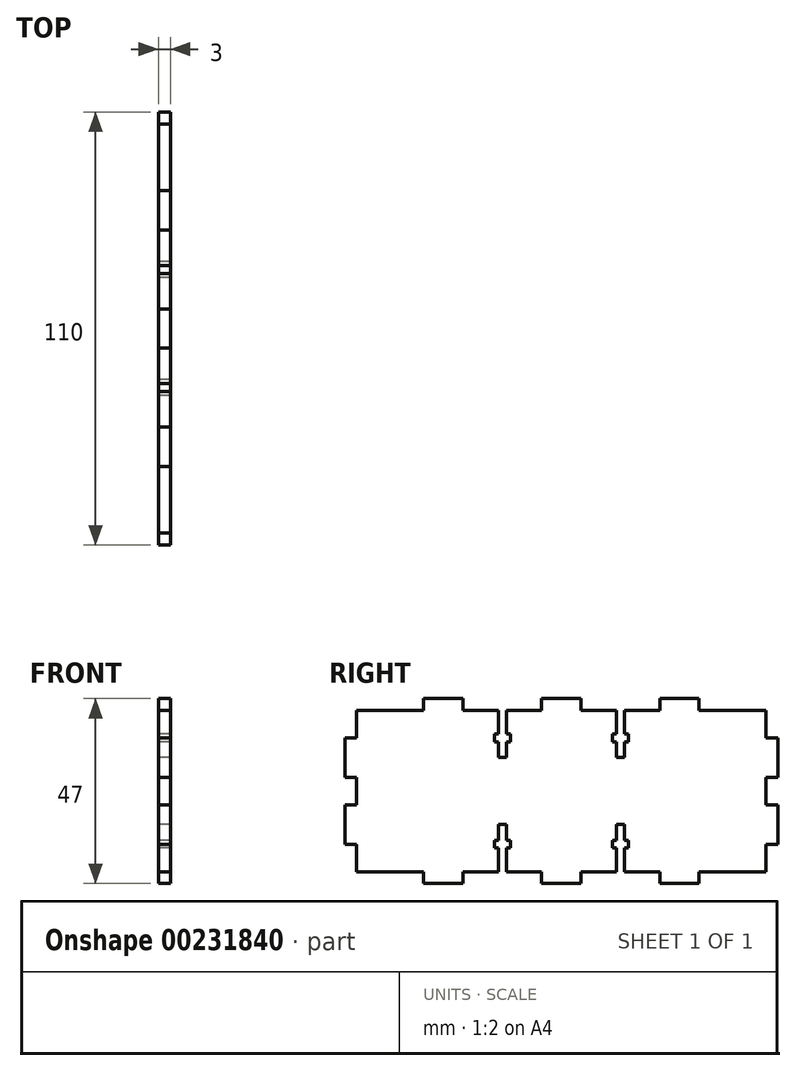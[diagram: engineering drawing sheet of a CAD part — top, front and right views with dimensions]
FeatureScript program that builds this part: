
annotation { "Feature Type Name" : "Feature", "Feature Type Description" : "" }
export const myFeature = defineFeature(function(context is Context, id is Id, definition is map)
    precondition{}
    {
        {
            var Q0;
            Q0=qCreatedBy(makeId("Right.planeOp"),FACE);
            var sketch = newSketch(context, id + "F0", { "sketchPlane" : qUnion([Q0])});
            skLineSegment(sketch, "E0", {"start": v(0, 0) * mm, "end": v(0, 7) * mm});
            skLineSegment(sketch, "E1", {"start": v(0, 7) * mm, "end": v(3, 7) * mm});
            skLineSegment(sketch, "E2", {"start": v(3, 7) * mm, "end": v(3, 17) * mm});
            skLineSegment(sketch, "E3", {"start": v(3, 17) * mm, "end": v(0, 17) * mm});
            skLineSegment(sketch, "E4", {"start": v(0, 17) * mm, "end": v(0, 24) * mm});
            skLineSegment(sketch, "E5", {"start": v(0, 24) * mm, "end": v(3, 24) * mm});
            skLineSegment(sketch, "E6", {"start": v(3, 24) * mm, "end": v(3, 34) * mm});
            skLineSegment(sketch, "E7", {"start": v(3, 34) * mm, "end": v(0, 34) * mm});
            skLineSegment(sketch, "E8", {"start": v(0, 34) * mm, "end": v(0, 41) * mm});
            skLineSegment(sketch, "E9", {"start": v(0, 41) * mm, "end": v(-17, 41) * mm});
            skLineSegment(sketch, "E10", {"start": v(-17, 41) * mm, "end": v(-17, 44) * mm});
            skLineSegment(sketch, "E11", {"start": v(-17, 44) * mm, "end": v(-27, 44) * mm});
            skLineSegment(sketch, "E12", {"start": v(-27, 44) * mm, "end": v(-27, 41) * mm});
            skLineSegment(sketch, "E13", {"start": v(-27, 41) * mm, "end": v(-36, 41) * mm});
            skLineSegment(sketch, "E14", {"start": v(-47, 41) * mm, "end": v(-47, 44) * mm});
            skLineSegment(sketch, "E15", {"start": v(-47, 44) * mm, "end": v(-52, 44) * mm});
            skLineSegment(sketch, "E16", {"start": v(-52, 44) * mm, "end": v(-52, -7.38) * mm, "construction": true});
            skLineSegment(sketch, "E17", {"start": v(0, 20.5) * mm, "end": v(-65.3, 20.5) * mm, "construction": true});
            skPoint(sketch, "E17.endSnap0", {"position": v(0, 20.5) * mm});
            skLineSegment(sketch, "E18.MirrorCS", {"start": v(-57, 41) * mm, "end": v(-57, 44) * mm});
            skLineSegment(sketch, "E19.MirrorCS", {"start": v(-77, 44) * mm, "end": v(-77, 41) * mm});
            skLineSegment(sketch, "E20.MirrorCS", {"start": v(-87, 41) * mm, "end": v(-87, 44) * mm});
            skLineSegment(sketch, "E21.MirrorCS", {"start": v(-57, 44) * mm, "end": v(-52, 44) * mm});
            skLineSegment(sketch, "E22.MirrorCS", {"start": v(-77, 41) * mm, "end": v(-68, 41) * mm});
            skLineSegment(sketch, "E23.MirrorCS", {"start": v(-87, 44) * mm, "end": v(-77, 44) * mm});
            skLineSegment(sketch, "E24.MirrorCS", {"start": v(-104, 41) * mm, "end": v(-87, 41) * mm});
            skLineSegment(sketch, "E25.MirrorCS", {"start": v(-104, 7) * mm, "end": v(-107, 7) * mm});
            skLineSegment(sketch, "E26.MirrorCS", {"start": v(-107, 17) * mm, "end": v(-104, 17) * mm});
            skLineSegment(sketch, "E27.MirrorCS", {"start": v(-104, 17) * mm, "end": v(-104, 24) * mm});
            skLineSegment(sketch, "E28.MirrorCS", {"start": v(-104, 24) * mm, "end": v(-107, 24) * mm});
            skLineSegment(sketch, "E29.MirrorCS", {"start": v(-107, 34) * mm, "end": v(-104, 34) * mm});
            skLineSegment(sketch, "E30.MirrorCS", {"start": v(-104, 0) * mm, "end": v(-104, 7) * mm});
            skLineSegment(sketch, "E31.MirrorCS", {"start": v(-107, 7) * mm, "end": v(-107, 17) * mm});
            skPoint(sketch, "E32.MirrorP", {"position": v(-104, 20.5) * mm});
            skLineSegment(sketch, "E33.MirrorCS", {"start": v(-107, 24) * mm, "end": v(-107, 34) * mm});
            skLineSegment(sketch, "E34.MirrorCS", {"start": v(-104, 34) * mm, "end": v(-104, 41) * mm});
            skLineSegment(sketch, "E35.MirrorCS", {"start": v(-47, 0) * mm, "end": v(-47, -3) * mm});
            skLineSegment(sketch, "E36.MirrorCS", {"start": v(-57, 0) * mm, "end": v(-57, -3) * mm});
            skLineSegment(sketch, "E37.MirrorCS", {"start": v(-27, -3) * mm, "end": v(-27, 0) * mm});
            skLineSegment(sketch, "E38.MirrorCS", {"start": v(-77, -3) * mm, "end": v(-77, 0) * mm});
            skLineSegment(sketch, "E39.MirrorCS", {"start": v(-87, 0) * mm, "end": v(-87, -3) * mm});
            skLineSegment(sketch, "E40.MirrorCS", {"start": v(-17, 0) * mm, "end": v(-17, -3) * mm});
            skLineSegment(sketch, "E41.MirrorCS", {"start": v(-47, -3) * mm, "end": v(-52, -3) * mm});
            skLineSegment(sketch, "E42.MirrorCS", {"start": v(0, 0) * mm, "end": v(-17, 0) * mm});
            skLineSegment(sketch, "E43.MirrorCS", {"start": v(-27, 0) * mm, "end": v(-36, 0) * mm});
            skLineSegment(sketch, "E44.MirrorCS", {"start": v(-87, -3) * mm, "end": v(-77, -3) * mm});
            skLineSegment(sketch, "E45.MirrorCS", {"start": v(-77, 0) * mm, "end": v(-68, 0) * mm});
            skLineSegment(sketch, "E46.MirrorCS", {"start": v(-57, -3) * mm, "end": v(-52, -3) * mm});
            skLineSegment(sketch, "E47.MirrorCS", {"start": v(-104, 0) * mm, "end": v(-87, 0) * mm});
            skLineSegment(sketch, "E48.MirrorCS", {"start": v(-17, -3) * mm, "end": v(-27, -3) * mm});
            skLineSegment(sketch, "E49", {"start": v(-37, 41) * mm, "end": v(-37, 14.7) * mm, "construction": true});
            skLineSegment(sketch, "E50.top", {"start": v(-38, 29) * mm, "end": v(-36, 29) * mm});
            skLineSegment(sketch, "E50.left", {"start": v(-38, 41) * mm, "end": v(-38, 35) * mm});
            skLineSegment(sketch, "E50.right", {"start": v(-36, 41) * mm, "end": v(-36, 35) * mm});
            skLineSegment(sketch, "E51.trimOffspring", {"start": v(-38, 41) * mm, "end": v(-47, 41) * mm});
            skLineSegment(sketch, "E52.bottom", {"start": v(-39, 35) * mm, "end": v(-38, 35) * mm});
            skLineSegment(sketch, "E52.top", {"start": v(-39, 33) * mm, "end": v(-38, 33) * mm});
            skLineSegment(sketch, "E52.left", {"start": v(-39, 35) * mm, "end": v(-39, 33) * mm});
            skLineSegment(sketch, "E52.right", {"start": v(-35, 35) * mm, "end": v(-35, 33) * mm});
            skLineSegment(sketch, "E53.trimOffspring", {"start": v(-36, 35) * mm, "end": v(-35, 35) * mm});
            skLineSegment(sketch, "E54.trimOffspring", {"start": v(-38, 33) * mm, "end": v(-38, 29) * mm});
            skLineSegment(sketch, "E55.trimOffspring", {"start": v(-36, 33) * mm, "end": v(-35, 33) * mm});
            skLineSegment(sketch, "E56.trimOffspring", {"start": v(-36, 33) * mm, "end": v(-36, 29) * mm});
            skLineSegment(sketch, "E57.MirrorCS", {"start": v(-65, 33) * mm, "end": v(-66, 33) * mm});
            skLineSegment(sketch, "E58.MirrorCS", {"start": v(-68, 35) * mm, "end": v(-69, 35) * mm});
            skLineSegment(sketch, "E59.MirrorCS", {"start": v(-65, 35) * mm, "end": v(-66, 35) * mm});
            skLineSegment(sketch, "E60.MirrorCS", {"start": v(-68, 33) * mm, "end": v(-69, 33) * mm});
            skLineSegment(sketch, "E61.MirrorCS", {"start": v(-69, 35) * mm, "end": v(-69, 33) * mm});
            skLineSegment(sketch, "E62.MirrorCS", {"start": v(-65, 35) * mm, "end": v(-65, 33) * mm});
            skLineSegment(sketch, "E63.MirrorCS", {"start": v(-66, 41) * mm, "end": v(-66, 35) * mm});
            skLineSegment(sketch, "E64.MirrorCS", {"start": v(-66, 29) * mm, "end": v(-68, 29) * mm});
            skLineSegment(sketch, "E65.MirrorCS", {"start": v(-68, 33) * mm, "end": v(-68, 29) * mm});
            skLineSegment(sketch, "E66.MirrorCS", {"start": v(-68, 41) * mm, "end": v(-68, 35) * mm});
            skLineSegment(sketch, "E67.MirrorCS", {"start": v(-66, 33) * mm, "end": v(-66, 29) * mm});
            skLineSegment(sketch, "E68.trimOffspring", {"start": v(-66, 41) * mm, "end": v(-57, 41) * mm});
            skLineSegment(sketch, "E69.MirrorCS", {"start": v(-36, 8) * mm, "end": v(-35, 8) * mm});
            skLineSegment(sketch, "E70.MirrorCS", {"start": v(-36, 6) * mm, "end": v(-35, 6) * mm});
            skLineSegment(sketch, "E71.MirrorCS", {"start": v(-39, 8) * mm, "end": v(-38, 8) * mm});
            skLineSegment(sketch, "E72.MirrorCS", {"start": v(-65, 6) * mm, "end": v(-66, 6) * mm});
            skLineSegment(sketch, "E73.MirrorCS", {"start": v(-38, 12) * mm, "end": v(-36, 12) * mm});
            skLineSegment(sketch, "E74.MirrorCS", {"start": v(-68, 8) * mm, "end": v(-69, 8) * mm});
            skLineSegment(sketch, "E75.MirrorCS", {"start": v(-68, 6) * mm, "end": v(-69, 6) * mm});
            skLineSegment(sketch, "E76.MirrorCS", {"start": v(-66, 12) * mm, "end": v(-68, 12) * mm});
            skLineSegment(sketch, "E77.MirrorCS", {"start": v(-65, 8) * mm, "end": v(-66, 8) * mm});
            skLineSegment(sketch, "E78.MirrorCS", {"start": v(-39, 6) * mm, "end": v(-38, 6) * mm});
            skLineSegment(sketch, "E79.MirrorCS", {"start": v(-35, 6) * mm, "end": v(-35, 8) * mm});
            skLineSegment(sketch, "E80.MirrorCS", {"start": v(-39, 6) * mm, "end": v(-39, 8) * mm});
            skLineSegment(sketch, "E81.MirrorCS", {"start": v(-38, 8) * mm, "end": v(-38, 12) * mm});
            skLineSegment(sketch, "E82.MirrorCS", {"start": v(-66, 0) * mm, "end": v(-66, 6) * mm});
            skLineSegment(sketch, "E83.MirrorCS", {"start": v(-36, 0) * mm, "end": v(-36, 6) * mm});
            skLineSegment(sketch, "E84.MirrorCS", {"start": v(-65, 6) * mm, "end": v(-65, 8) * mm});
            skLineSegment(sketch, "E85.MirrorCS", {"start": v(-68, 0) * mm, "end": v(-68, 6) * mm});
            skLineSegment(sketch, "E86.MirrorCS", {"start": v(-69, 6) * mm, "end": v(-69, 8) * mm});
            skLineSegment(sketch, "E87.MirrorCS", {"start": v(-66, 0) * mm, "end": v(-57, 0) * mm});
            skLineSegment(sketch, "E88.MirrorCS", {"start": v(-36, 8) * mm, "end": v(-36, 12) * mm});
            skLineSegment(sketch, "E89.MirrorCS", {"start": v(-38, 0) * mm, "end": v(-47, 0) * mm});
            skLineSegment(sketch, "E90.MirrorCS", {"start": v(-68, 8) * mm, "end": v(-68, 12) * mm});
            skLineSegment(sketch, "E91.MirrorCS", {"start": v(-38, 0) * mm, "end": v(-38, 6) * mm});
            skLineSegment(sketch, "E92.MirrorCS", {"start": v(-66, 8) * mm, "end": v(-66, 12) * mm});
            skSolve(sketch);
        }
        {
            var Q0;
            Q0 = qSketchRegion(id + "F0", true);
            extrude(context, id + "F1", {"entities" : qUnion([Q0]), "depth" : 3 * mm});
        }
    });
